FCSTD DOCUMENT  (FreeCAD 0.18R15340 (Git))
Label: SugarGroveRd
License: All rights reserved
LicenseURL: http://en.wikipedia.org/wiki/All_rights_reserved
objects: Part::Part2DObjectPython×5, Image::ImagePlane×1, Sketcher::SketchObject×1
note: 6 computed .brp shape members not serialized (recipe doc carries the construction recipe); baked Part::Feature solids carry a one-line shape summary decoded from their .brp

FEATURE [Image::ImagePlane] ImagePlane
  Placement = pos=(426720,-408432,-304.8) rot=(0,0,1;0rad)
  XSize = 914400
  YSize = 914400
FEATURE [Part::Part2DObjectPython] Test_Horiz  label="PI_Wire"  # Draft 2D object (typed FeaturePython)
  ChamferSize = 0
  Closed = false
  Datum = (0,0,0)
  End = (876227,-862449,0)
  FilletRadius = 0
  Geometry = (5) [(0,0,0),(184415,-214859,0),(750425,-206132,0),(743091,-718189,0),(876227,-862449,0)]
  ID = Test
  Intersection_Equation = (0,0,0)
  Length = 1.55764e+06
  MakeFace = true
  Points = (5) [(0,0,0),(184415,-214859,0),(750425,-206132,0),(743091,-718189,0),(876227,-862449,0)]
  Start = (0,0,0)
  Subdivisions = 0
  Units = English
FEATURE [Part::Part2DObjectPython] Test_Horiz001  label="PI_Spline"  # Draft 2D object (typed FeaturePython)
  Closed = false
  Datum = (0,0,0)
  Geometry = (5) [(0,0,0),(184415,-214859,0),(750425,-206132,0),(743091,-718189,0),(876227,-862449,0)]
  ID = Test
  Intersection_Equation = (0,0,0)
  MakeFace = true
  Parameterization = 1
  Points = (5) [(0,0,0),(184415,-214859,0),(750425,-206132,0),(743091,-718189,0),(876227,-862449,0)]
  Units = English
FEATURE [Part::Part2DObjectPython] Sugar_Grove_Road_Horiz  # Draft 2D object (typed FeaturePython)
  Alignment_Equations = (1) [(0,50000,0)]
  ChamferSize = 0
  Closed = false
  Datum = (0,0,0)
  End = (0,0,0)
  FilletRadius = 0
  Geometry = 930.0, 139.3986, 670.0, 0.0 | 1850.0, 89.0825, 669.9999999647122, 0.0 | 1680.0, 180.5808, 670.0, 0.0 | 644.048, 137.29639, 0.0, 0.0
  ID = Sugar_Grove_Road
  Intersection_Equation = (0,0,0)
  Length = 1.44199e+06
  MakeFace = true
  Method = 0
  PIs = (5) [(0,0,0),(184476,-215222,0),(748284,-206192,0),(743093,-718230,0),(876229,-862490,0)]
  Points = (36) [(0,0,0),(122056,-142398,0),(137476,-158517,0),(154563,-172857,0),(173111,-185248,0),(192901,-195542,0),(213695,-203617,0),(235245,-209375,0),+28 more]
  Seg_Value = 1
  Start = (0,0,0)
  Subdivisions = 0
  Units = English
FEATURE [Part::Part2DObjectPython] Penrose_Road_W_Horiz  # Draft 2D object (typed FeaturePython)
  Alignment_Equations = (1) [(0,1000,0)]
  ChamferSize = 0
  Closed = false
  Datum = (0,0,0)
  End = (0,0,0)
  FilletRadius = 0
  Geometry = 154.097, 244.64028, 175.0, 0.0 | 559.026, 270.0, 0.0, 0.0
  ID = Penrose_Road_W
  Intersection_Equation = (50909,1000,0)
  Length = 216923
  MakeFace = true
  Method = 0
  PIs = (3) [(0,0,0),(-42442.7,-20116.7,0),(-212834,-20116.7,0)]
  Parent_Alignment = -> Sugar_Grove_Road_Horiz
  Placement = pos=(193168,-195646,0) rot=(0,0,1;0rad)
  Points = (6) [(0,0,0),(-31598.2,-14976.7,0),(-42350.9,-18727.9,0),(-53654.9,-20110.9,0),(-54443.7,-20116.7,0),(-212834,-20116.7,0)]
  Seg_Value = 1
  Start = (0,0,0)
  Subdivisions = 0
  Units = English
FEATURE [Part::Part2DObjectPython] Penrose_Road_E_Horiz  # Draft 2D object (typed FeaturePython)
  Alignment_Equations = (1) [(0,2000,0)]
  ChamferSize = 0
  Closed = false
  Datum = (0,0,0)
  End = (0,0,0)
  FilletRadius = 0
  Geometry = 429.658, 270.0, 175.0, 0.0 | 312.032, 224.9725, 0.0, 0.0
  ID = Penrose_Road_E
  Intersection_Equation = (52586.2,3008.87,0)
  Length = 223696
  MakeFace = true
  Method = 0
  PIs = (3) [(0,0,0),(-130960,-2.40569e-11,0),(-198179,-67283.3,0)]
  Parent_Alignment = -> Sugar_Grove_Road_Horiz
  Placement = pos=(884037,-201927,0) rot=(0,0,1;0rad)
  Points = (7) [(0,0,0),(-108851,-1.99955e-11,0),(-120174,-1215.72,0),(-130981,-4807.45,0),(-140779,-10611.5,0),(-146586,-15641,0),(-198179,-67283.3,0)]
  Seg_Value = 1
  Start = (0,0,0)
  Subdivisions = 0
  Units = English
FEATURE [Sketcher::SketchObject] Sketch
  AttachmentOffset = pos=(0,0,609.6) rot=(0,0,1;0rad)
  ExternalGeometry = -> [Penrose_Road_E_Horiz]
  Support = -> [ImagePlane]
  sketch-geometry (16):
    g0: LineSegment StartX=0 StartY=0 StartZ=0 EndX=184415 EndY=-214859 EndZ=0
    g1: LineSegment StartX=184415 StartY=-214859 StartZ=0 EndX=750427 EndY=-206175 EndZ=0
    g2: LineSegment StartX=750427 StartY=-206175 StartZ=0 EndX=743094 EndY=-718232 EndZ=0
    g3: LineSegment StartX=876229 StartY=-862492 StartZ=0 EndX=743094 EndY=-718232 EndZ=0
    g4: ArcOfCircle CenterX=276955 CenterY=-9337.1 CenterZ=0 NormalX=0 NormalY=0 NormalZ=1 AngleXU=0 Radius=204078 StartAngle=3.85089 EndAngle=4.72773
    g5: ArcOfCircle CenterX=544016 CenterY=-412797 CenterZ=0 NormalX=0 NormalY=0 NormalZ=1 AngleXU=0 Radius=203431 StartAngle=6.26886 EndAngle=7.86932
    g6: ArcOfCircle CenterX=942297 CenterY=-641998 CenterZ=0 NormalX=0 NormalY=0 NormalZ=1 AngleXU=0 Radius=198091 StartAngle=3.12727 EndAngle=3.88691
    g7: LineSegment StartX=276955 StartY=-9337.1 StartZ=0 EndX=184415 EndY=-214859 EndZ=0
    g8: LineSegment StartX=276955 StartY=-9337.1 StartZ=0 EndX=276955 EndY=106888 EndZ=0
    g9: LineSegment StartX=122097 StartY=-142253 StartZ=0 EndX=276955 EndY=-9337.1 EndZ=0
    g10: LineSegment StartX=737451 StartY=-217568 StartZ=0 EndX=775186 EndY=-255267 EndZ=0
    g11: LineSegment StartX=775186 StartY=-201927 StartZ=0 EndX=775186 EndY=-255267 EndZ=0
    g12: LineSegment [constr] StartX=775186 StartY=-201927 StartZ=0 EndX=775186 EndY=-116660 EndZ=0
    g13: LineSegment [constr] StartX=737451 StartY=-217568 StartZ=0 EndX=737451 EndY=-148122 EndZ=0
    g14: LineSegment [constr] StartX=737451 StartY=-217568 StartZ=0 EndX=753077 EndY=-201927 EndZ=0
    g15: LineSegment [constr] StartX=775186 StartY=-201927 StartZ=0 EndX=753077 EndY=-201927 EndZ=0
  constraints (52):
    c: Coincident(g0,g-1)
    c: Coincident(g0,g1)
    c: Coincident(g1,g2)
    c: Coincident(g2,g3)
    c: Block(g0)
    c: Block(g1)
    c: Block(g2)
    c: Block(g3)
    c: Tangent(g4,g1) = -1.5708
    c: Tangent(g4,g0) = -1.5708
    c: Tangent(g6,g2) = -1.5708
    c: Tangent(g6,g3) = 1.5708
    c: Tangent(g5,g1) = 1.5708
    c: Tangent(g5,g2) = 1.5708
    c: Distance(g0,g0) = 283149
    c: Distance(g0,g1) = 566079
    c: Distance(g1,g2) = 512109
    c: Distance(g2,g3) = 196306
    c: Radius(g4) = 204078
    c: Radius(g5) = 203431
    c: Radius(g6) = 198091
    c: Angle(g0,g-2) = 2.4323
    c: Angle(g1,g-2) = 1.55546
    c: Angle(g2,g-2) = 0.014321
    c: Angle(g-2,g3) = 0.745318
    c: Coincident(g7,g4)
    c: Coincident(g7,g0)
    c: Coincident(g8,g4)
    c: Vertical(g8)
    c: Angle(g8,g7) = 2.71851
    c: Coincident(g9,g4)
    c: Coincident(g9,g4)
    c: Angle(g8,g9) = 2.28009
    c: Coincident(g10,g-4)
    c: Coincident(g11,g-3)
    c: Coincident(g11,g10)
    c: Perpendicular(g-3,g11)
    c: Perpendicular(g-4,g10)
    c: Angle(g11,g-3) = 1.5708
    c: Angle(g-4,g10) = 1.5708
    c: Coincident(g12,g11)
    c: Vertical(g12)
    c: Angle(g-3,g12) = 1.5708
    c: Coincident(g13,g10)
    c: Vertical(g13)
    c: Angle(g10,g13) = 2.35571
    c: Distance(g-3) = 108851
    c: Coincident(g14,g10)
    c: Coincident(g15,g11)
    c: Coincident(g15,g14)
    c: Parallel(g15,g-3)
    c: Parallel(g14,g-4)
